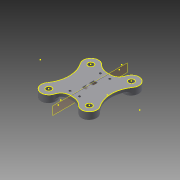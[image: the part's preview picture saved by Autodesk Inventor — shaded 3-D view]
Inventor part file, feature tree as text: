
AUTODESK INVENTOR PART (.ipt)
format: ipt  version: 2014 (Build 180170000, 170)  size: 802,816 bytes
history: native  units: in
note: dims shown in document units (in); Inventor stores cm internally (conversion verified against a paired STEP export)
features: fillet x8, extrude x7, sketch x7, chamfer x2, plane x1, mirror x1
ambient origin geometry x8: Origin, YZ Plane, XZ Plane, XY Plane, X Axis, Y Axis, Z Axis, Center Point
bodies: Body1 (feature_tree)
feature tree (26):
  extrude  "Extrusion12"  Depth=1.0441in
  extrude  "Extrusion13"  Depth=2.3622in
  sketch  "Sketch13"  dims[d2=1.5748in d5=2.3622in]
  plane  "Work Plane2"
  extrude  "Extrusion14"  Depth=0.9843in
  extrude  "Extrusion15"  Depth=0.9449in
  mirror  "Mirror2"
  extrude  "Extrusion16"  Depth=0.2362in TaperAngle=0.0deg
  extrude  "Extrusion17"  Depth=0.2362in TaperAngle=0.0deg
  extrude  "Extrusion18"  Depth=0.0197in
  chamfer  "Chamfer1"  Distance=0.3346in
  chamfer  "Chamfer2"  Distance=0.1181in
  fillet  "Fillet8"  Radius=1.1811in
  fillet  "Fillet9"  Radius=0.0591in
  fillet  "Fillet10"  Radius=0.1181in
  fillet  "Fillet11"  Radius=0.0394in
  fillet  "Fillet12"  Radius=0.1181in
  fillet  "Fillet13"  Radius=0.1575in
  fillet  "Fillet14"  Radius=0.1575in
  fillet  "Fillet15"  Radius=0.2362in
  sketch  "Sketch12"  dims[d0=1.1713in d1=1.0441in]
  sketch  "Sketch14"  dims[d6=0.1969in d7=0.9843in]
  sketch  "Sketch15"  dims[d64=0.3543in d65=0.9449in]
  sketch  "Sketch16"  dims[d66=1.7717in d70=0.2362in d71=0.0in]
  sketch  "Sketch17"  dims[d72=0.5512in d73=0.2362in d74=0.0in]
  sketch  "Sketch18"  dims[d75=0.0in d76=0.5945in d77=0.3346in d78=0.1181in d79=1.1811in d80=0.0in d81=0.0591in d82=0.1181in d83=0.0in d84=0.0394in d85=0.1181in d86=0.0in d87=0.1575in d88=0.1575in d89=0.2362in d90=0.0in d91=0.4724in d92=0.1417in d93=1.8898in d94=0.5906in d95=0.2362in d96=0.0in d97=0.0787in d98=0.0787in d99=45.0deg d100=0.0787in d101=0.0787in d102=45.0deg d103=0.0394in d104=0.0394in d105=0.0394in d106=0.0197in d107=0.0197in d108=0.0197in d109=0.0197in d110=0.0197in]
